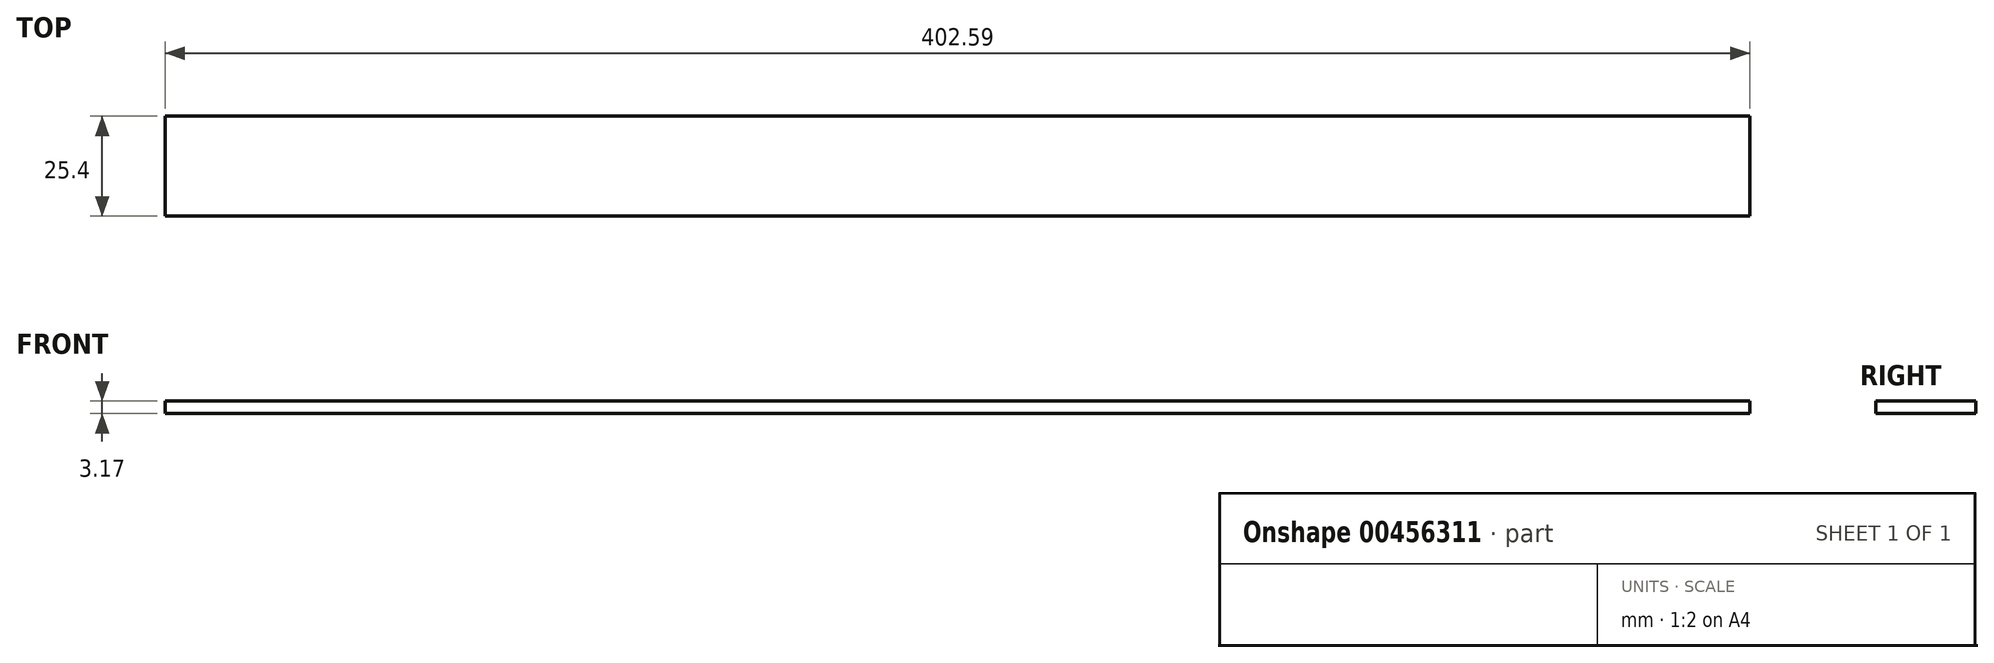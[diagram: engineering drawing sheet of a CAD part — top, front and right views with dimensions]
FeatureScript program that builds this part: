
annotation { "Feature Type Name" : "Feature", "Feature Type Description" : "" }
export const myFeature = defineFeature(function(context is Context, id is Id, definition is map)
    precondition{}
    {
        {
            var Q0;
            Q0=qCreatedBy(makeId("Top.planeOp"),FACE);
            var sketch = newSketch(context, id + "F0", { "sketchPlane" : qUnion([Q0])});
            skLineSegment(sketch, "E0.bottom", {"start": v(0, 0) * mm, "end": v(402.59, 0) * mm});
            skLineSegment(sketch, "E0.top", {"start": v(0, 25.4) * mm, "end": v(402.59, 25.4) * mm});
            skLineSegment(sketch, "E0.left", {"start": v(0, 0) * mm, "end": v(0, 25.4) * mm});
            skLineSegment(sketch, "E0.right", {"start": v(402.6, 0) * mm, "end": v(402.6, 25.4) * mm});
            skSolve(sketch);
        }
        {
            var Q0;
            Q0=makeQuery(id+"F0.imprint","IMPRINT",FACE,{"disambiguationData":[TD([[makeQuery(id+"F0.imprint","IMPRINT",EDGE,{"derivedFrom":sQuery(id+"F0.wireOp",EDGE,"E0.bottom")}),1.0]])]});
            extrude(context, id + "F1", {"entities" : qUnion([Q0]), "depth" : 3.17 * mm});
        }
    });
